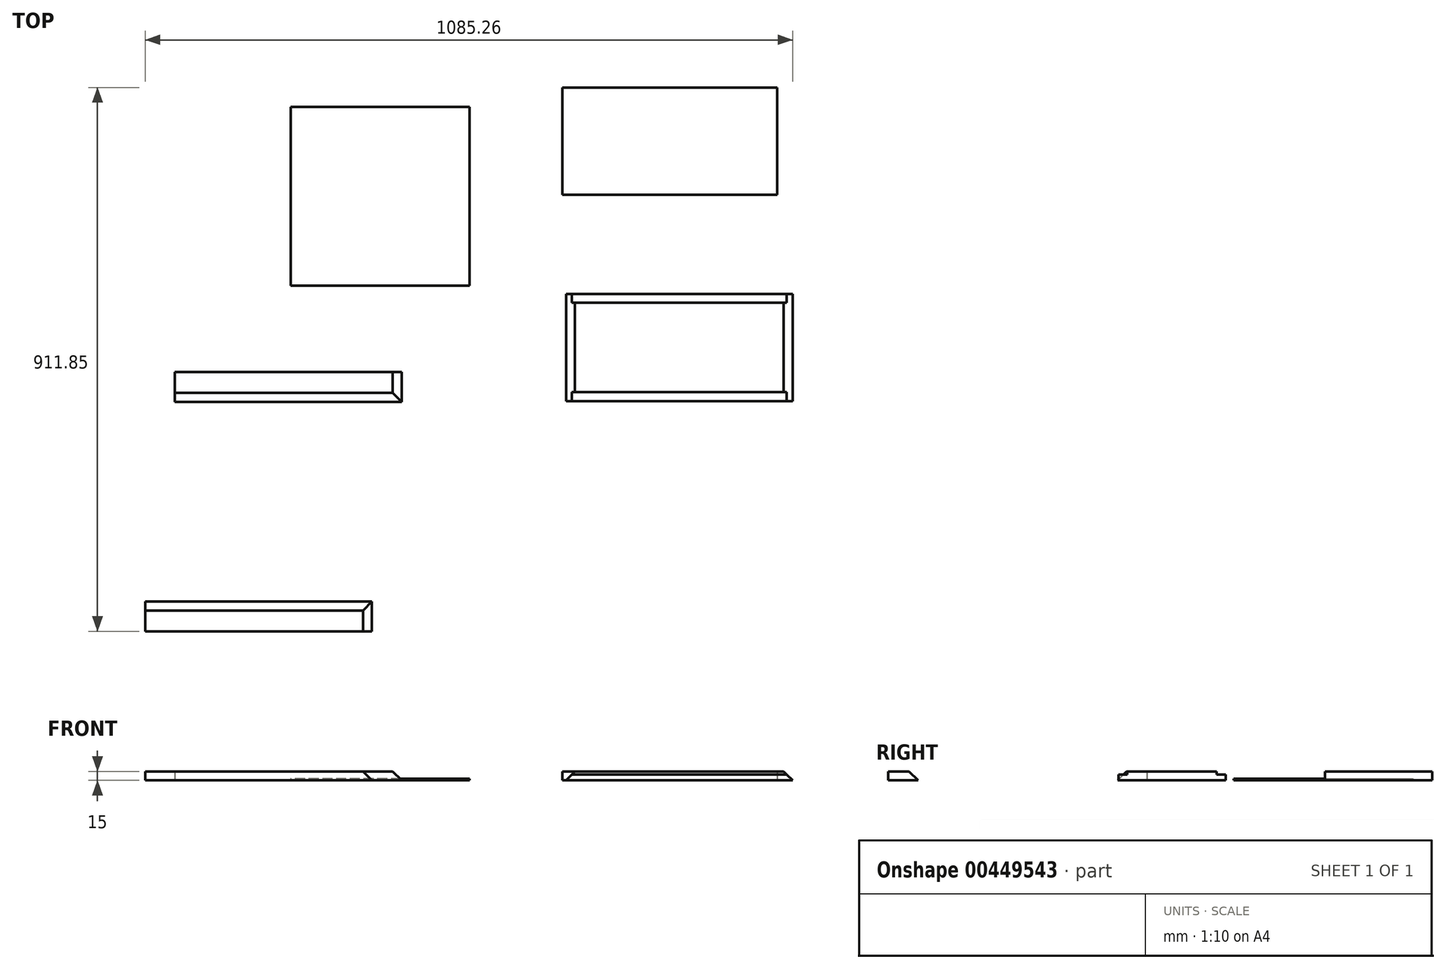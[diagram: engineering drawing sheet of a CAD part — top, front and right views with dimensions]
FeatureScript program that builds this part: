
annotation { "Feature Type Name" : "Feature", "Feature Type Description" : "" }
export const myFeature = defineFeature(function(context is Context, id is Id, definition is map)
    precondition{}
    {
        {
            var Q0;
            Q0=qCreatedBy(makeId("Top.planeOp"),FACE);
            var sketch = newSketch(context, id + "F0", { "sketchPlane" : qUnion([Q0])});
            skLineSegment(sketch, "E0.bottom", {"start": v(104.54, -6.9) * mm, "end": v(-255.46, -6.9) * mm});
            skLineSegment(sketch, "E0.top", {"start": v(104.54, 173.1) * mm, "end": v(-255.46, 173.1) * mm});
            skLineSegment(sketch, "E0.left", {"start": v(104.54, -6.9) * mm, "end": v(104.54, 173.1) * mm});
            skLineSegment(sketch, "E0.right", {"start": v(-255.46, -6.9) * mm, "end": v(-255.46, 173.1) * mm});
            skSolve(sketch);
        }
        {
            var Q0;
            Q0 = qSketchRegion(id + "F0", true);
            extrude(context, id + "F1", {"entities" : qUnion([Q0]), "depth" : 15 * mm});
        }
        {
            var Q0;
            Q0=qCreatedBy(makeId("Top.planeOp"),FACE);
            var sketch = newSketch(context, id + "F2", { "sketchPlane" : qUnion([Q0])});
            skLineSegment(sketch, "E1.bottom", {"start": v(-234.67, -172.9) * mm, "end": v(115.33, -172.9) * mm});
            skLineSegment(sketch, "E1.top", {"start": v(-234.67, -352.9) * mm, "end": v(115.33, -352.9) * mm});
            skLineSegment(sketch, "E1.left", {"start": v(-234.67, -172.9) * mm, "end": v(-234.67, -352.9) * mm});
            skLineSegment(sketch, "E1.right", {"start": v(115.33, -172.9) * mm, "end": v(115.33, -352.9) * mm});
            skSolve(sketch);
        }
        {
            var Q0;
            Q0 = qSketchRegion(id + "F2", true);
            extrude(context, id + "F3", {"entities" : qUnion([Q0]), "depth" : 15 * mm});
        }
        {
            var Q0;
            Q0=makeQuery(id+"F3.opExtrude","SWEPT_FACE",FACE,{"disambiguationData":[OSD([sQuery(id+"F2.wireOp",EDGE,"E1.top")])]});
            var sketch = newSketch(context, id + "F4", { "sketchPlane" : qUnion([Q0])});
            skLineSegment(sketch, "E2", {"start": v(-234.67, 0) * mm, "end": v(-249.67, 0) * mm});
            skLineSegment(sketch, "E3", {"start": v(-249.67, 0) * mm, "end": v(-234.67, 15) * mm});
            skLineSegment(sketch, "E4", {"start": v(115.33, 0) * mm, "end": v(130.33, 0) * mm});
            skLineSegment(sketch, "E5", {"start": v(130.33, 0) * mm, "end": v(115.33, 15) * mm});
            skSolve(sketch);
        }
        {
            var Q0;
            Q0 = qSketchRegion(id + "F4", true);
            var Q1;
            Q1=makeQuery(id+"F4.imprint","IMPRINT",FACE,{"disambiguationData":[TD([[makeQuery(id+"F4.imprint","IMPRINT",EDGE,{"derivedFrom":sQuery(id+"F4.wireOp",EDGE,"E2")}),-1.0]])]});
            var Q2;
            Q2=makeQuery(id+"F4.imprint","IMPRINT",FACE,{"disambiguationData":[TD([[makeQuery(id+"F4.imprint","IMPRINT",EDGE,{"derivedFrom":sQuery(id+"F4.wireOp",EDGE,"E4")}),1.0]])]});
            extrude(context, id + "F5", {"entities" : qUnion([Q0, Q1, Q2]), "operationType" : NewBodyOperationType.ADD, "oppositeDirection" : true, "depth" : 180 * mm});
        }
        {
            var Q0;
            Q0=makeQuery(id+"F3.opExtrude","CAP_FACE",FACE,{"disambiguationData":[OSD([sQuery(id+"F2.wireOp",EDGE,"E1.bottom"),sQuery(id+"F2.wireOp",EDGE,"E1.top"),sQuery(id+"F2.wireOp",EDGE,"E1.left"),sQuery(id+"F2.wireOp",EDGE,"E1.right")])],"isStart":false});
            var sketch = newSketch(context, id + "F6", { "sketchPlane" : qUnion([Q0])});
            skLineSegment(sketch, "E6.bottom", {"start": v(-234.67, -172.9) * mm, "end": v(115.33, -172.9) * mm});
            skLineSegment(sketch, "E6.top", {"start": v(-234.67, -187.9) * mm, "end": v(115.33, -187.9) * mm});
            skLineSegment(sketch, "E6.left", {"start": v(-234.67, -172.9) * mm, "end": v(-234.67, -187.9) * mm});
            skLineSegment(sketch, "E6.right", {"start": v(115.33, -172.9) * mm, "end": v(115.33, -187.9) * mm});
            skLineSegment(sketch, "E7.bottom", {"start": v(115.33, -187.9) * mm, "end": v(191.16, -187.9) * mm});
            skLineSegment(sketch, "E7.top", {"start": v(115.33, -172.9) * mm, "end": v(191.16, -172.9) * mm});
            skLineSegment(sketch, "E7.left", {"start": v(115.33, -187.9) * mm, "end": v(115.33, -172.9) * mm});
            skLineSegment(sketch, "E7.right", {"start": v(191.16, -187.9) * mm, "end": v(191.16, -172.9) * mm});
            skPoint(sketch, "E8.oppositeSnap0", {"position": v(-59.67, -172.9) * mm});
            skLineSegment(sketch, "E8.bottom", {"start": v(-234.67, -187.9) * mm, "end": v(-273.5, -187.9) * mm});
            skLineSegment(sketch, "E8.top", {"start": v(-234.67, -172.9) * mm, "end": v(-273.5, -172.9) * mm});
            skLineSegment(sketch, "E8.left", {"start": v(-234.67, -187.9) * mm, "end": v(-234.67, -172.9) * mm});
            skLineSegment(sketch, "E8.right", {"start": v(-273.5, -187.9) * mm, "end": v(-273.5, -172.9) * mm});
            skSolve(sketch);
        }
        {
            var Q0;
            Q0 = qSketchRegion(id + "F6", true);
            extrude(context, id + "F7", {"entities" : qUnion([Q0]), "operationType" : NewBodyOperationType.REMOVE, "oppositeDirection" : true, "depth" : 5 * mm});
        }
        {
            var Q0;
            Q0=makeQuery(id+"F3.opExtrude","CAP_FACE",FACE,{"disambiguationData":[OSD([sQuery(id+"F2.wireOp",EDGE,"E1.bottom"),sQuery(id+"F2.wireOp",EDGE,"E1.top"),sQuery(id+"F2.wireOp",EDGE,"E1.left"),sQuery(id+"F2.wireOp",EDGE,"E1.right")])],"isStart":false});
            var sketch = newSketch(context, id + "F8", { "sketchPlane" : qUnion([Q0])});
            skLineSegment(sketch, "E9.bottom", {"start": v(-234.67, -352.9) * mm, "end": v(115.33, -352.9) * mm});
            skLineSegment(sketch, "E9.top", {"start": v(-234.67, -337.9) * mm, "end": v(115.33, -337.9) * mm});
            skLineSegment(sketch, "E9.left", {"start": v(-234.67, -352.9) * mm, "end": v(-234.67, -337.9) * mm});
            skLineSegment(sketch, "E9.right", {"start": v(115.33, -352.9) * mm, "end": v(115.33, -337.9) * mm});
            skLineSegment(sketch, "E10.bottom", {"start": v(-234.67, -337.9) * mm, "end": v(-292.29, -337.9) * mm});
            skLineSegment(sketch, "E10.top", {"start": v(-234.67, -352.9) * mm, "end": v(-292.29, -352.9) * mm});
            skLineSegment(sketch, "E10.left", {"start": v(-234.67, -337.9) * mm, "end": v(-234.67, -352.9) * mm});
            skLineSegment(sketch, "E10.right", {"start": v(-292.29, -337.9) * mm, "end": v(-292.29, -352.9) * mm});
            skLineSegment(sketch, "E11.bottom", {"start": v(115.33, -337.9) * mm, "end": v(169.6, -337.9) * mm});
            skLineSegment(sketch, "E11.top", {"start": v(115.33, -352.9) * mm, "end": v(169.6, -352.9) * mm});
            skLineSegment(sketch, "E11.left", {"start": v(115.33, -337.9) * mm, "end": v(115.33, -352.9) * mm});
            skLineSegment(sketch, "E11.right", {"start": v(169.6, -337.9) * mm, "end": v(169.6, -352.9) * mm});
            skSolve(sketch);
        }
        {
            var Q0;
            Q0 = qSketchRegion(id + "F8", true);
            extrude(context, id + "F9", {"entities" : qUnion([Q0]), "operationType" : NewBodyOperationType.REMOVE, "oppositeDirection" : true, "depth" : 5 * mm});
        }
        {
            var Q0;
            Q0=qCreatedBy(makeId("Top.planeOp"),FACE);
            var sketch = newSketch(context, id + "F10", { "sketchPlane" : qUnion([Q0])});
            skLineSegment(sketch, "E12.bottom", {"start": v(-411.2, -159.37) * mm, "end": v(-711.2, -159.37) * mm});
            skLineSegment(sketch, "E12.top", {"start": v(-411.2, 140.63) * mm, "end": v(-711.2, 140.63) * mm});
            skLineSegment(sketch, "E12.left", {"start": v(-411.2, -159.37) * mm, "end": v(-411.2, 140.63) * mm});
            skLineSegment(sketch, "E12.right", {"start": v(-711.2, -159.37) * mm, "end": v(-711.2, 140.63) * mm});
            skSolve(sketch);
        }
        {
            var Q0;
            Q0 = qSketchRegion(id + "F10", true);
            extrude(context, id + "F11", {"entities" : qUnion([Q0]), "depth" : 3 * mm});
        }
        {
            var Q0;
            Q0=qCreatedBy(makeId("Top.planeOp"),FACE);
            var sketch = newSketch(context, id + "F12", { "sketchPlane" : qUnion([Q0])});
            skLineSegment(sketch, "E13.bottom", {"start": v(-525.04, -354.14) * mm, "end": v(-905.04, -354.14) * mm});
            skLineSegment(sketch, "E13.top", {"start": v(-525.04, -304.14) * mm, "end": v(-905.04, -304.14) * mm});
            skLineSegment(sketch, "E13.left", {"start": v(-525.04, -354.14) * mm, "end": v(-525.04, -304.14) * mm});
            skLineSegment(sketch, "E13.right", {"start": v(-905.04, -354.14) * mm, "end": v(-905.04, -304.14) * mm});
            skSolve(sketch);
        }
        {
            var Q0;
            Q0 = qSketchRegion(id + "F12", true);
            extrude(context, id + "F13", {"entities" : qUnion([Q0]), "depth" : 15 * mm});
        }
        {
            var Q0;
            Q0=makeQuery(id+"F13.opExtrude","SWEPT_FACE",FACE,{"disambiguationData":[OSD([sQuery(id+"F12.wireOp",EDGE,"E13.left")])]});
            var sketch = newSketch(context, id + "F14", { "sketchPlane" : qUnion([Q0])});
            skLineSegment(sketch, "E14.bottom", {"start": v(-354.14, 0) * mm, "end": v(-339.14, 0) * mm});
            skLineSegment(sketch, "E14.top", {"start": v(-354.14, 15) * mm, "end": v(-339.14, 15) * mm});
            skLineSegment(sketch, "E14.left", {"start": v(-354.14, 0) * mm, "end": v(-354.14, 15) * mm});
            skLineSegment(sketch, "E14.right", {"start": v(-339.14, 0) * mm, "end": v(-339.14, 15) * mm});
            skLineSegment(sketch, "E15", {"start": v(-354.14, 0) * mm, "end": v(-339.14, 15) * mm});
            skSolve(sketch);
        }
        {
            var Q0;
            Q0=makeQuery(id+"F14.imprint","IMPRINT",FACE,{"disambiguationData":[TD([[makeQuery(id+"F14.imprint","IMPRINT",EDGE,{"derivedFrom":sQuery(id+"F14.wireOp",EDGE,"E14.top")}),-1.0]])]});
            extrude(context, id + "F15", {"entities" : qUnion([Q0]), "operationType" : NewBodyOperationType.REMOVE, "oppositeDirection" : true, "depth" : 551 * mm});
        }
        {
            var Q0;
            Q0=makeQuery(id+"F13.opExtrude","SWEPT_FACE",FACE,{"disambiguationData":[OSD([sQuery(id+"F12.wireOp",EDGE,"E13.top")])]});
            var sketch = newSketch(context, id + "F16", { "sketchPlane" : qUnion([Q0])});
            skLineSegment(sketch, "E16.bottom", {"start": v(525.04, 0) * mm, "end": v(540.04, 0) * mm});
            skLineSegment(sketch, "E16.top", {"start": v(525.04, 15) * mm, "end": v(540.04, 15) * mm});
            skLineSegment(sketch, "E16.left", {"start": v(525.04, 0) * mm, "end": v(525.04, 15) * mm});
            skLineSegment(sketch, "E16.right", {"start": v(540.04, 0) * mm, "end": v(540.04, 15) * mm});
            skLineSegment(sketch, "E17", {"start": v(525.04, 0) * mm, "end": v(540.04, 15) * mm});
            skSolve(sketch);
        }
        {
            var Q0;
            Q0=makeQuery(id+"F16.imprint","IMPRINT",FACE,{"disambiguationData":[TD([[makeQuery(id+"F16.imprint","IMPRINT",EDGE,{"derivedFrom":sQuery(id+"F16.wireOp",EDGE,"E16.top")}),-1.0]])]});
            extrude(context, id + "F17", {"entities" : qUnion([Q0]), "operationType" : NewBodyOperationType.REMOVE, "oppositeDirection" : true, "depth" : 79 * mm});
        }
        {
            var Q0;
            Q0=qCreatedBy(makeId("Top.planeOp"),FACE);
            var sketch = newSketch(context, id + "F18", { "sketchPlane" : qUnion([Q0])});
            skLineSegment(sketch, "E18.bottom", {"start": v(-574.93, -688.75) * mm, "end": v(-954.93, -688.75) * mm});
            skLineSegment(sketch, "E18.top", {"start": v(-574.93, -738.75) * mm, "end": v(-954.93, -738.75) * mm});
            skLineSegment(sketch, "E18.left", {"start": v(-574.93, -688.75) * mm, "end": v(-574.93, -738.75) * mm});
            skLineSegment(sketch, "E18.right", {"start": v(-954.93, -688.75) * mm, "end": v(-954.93, -738.75) * mm});
            skSolve(sketch);
        }
        {
            var Q0;
            Q0 = qSketchRegion(id + "F18", true);
            extrude(context, id + "F19", {"entities" : qUnion([Q0]), "depth" : 15 * mm});
        }
        {
            var Q0;
            Q0=makeQuery(id+"F19.opExtrude","SWEPT_FACE",FACE,{"disambiguationData":[OSD([sQuery(id+"F18.wireOp",EDGE,"E18.bottom")])]});
            var sketch = newSketch(context, id + "F20", { "sketchPlane" : qUnion([Q0])});
            skLineSegment(sketch, "E19.bottom", {"start": v(574.93, 0) * mm, "end": v(589.93, 0) * mm});
            skLineSegment(sketch, "E19.top", {"start": v(574.93, 15) * mm, "end": v(589.93, 15) * mm});
            skLineSegment(sketch, "E19.left", {"start": v(574.93, 0) * mm, "end": v(574.93, 15) * mm});
            skLineSegment(sketch, "E19.right", {"start": v(589.93, 0) * mm, "end": v(589.93, 15) * mm});
            skLineSegment(sketch, "E20", {"start": v(574.93, 0) * mm, "end": v(589.93, 15) * mm});
            skSolve(sketch);
        }
        {
            var Q0;
            Q0=makeQuery(id+"F20.imprint","IMPRINT",FACE,{"disambiguationData":[TD([[makeQuery(id+"F20.imprint","IMPRINT",EDGE,{"derivedFrom":sQuery(id+"F20.wireOp",EDGE,"E19.top")}),-1.0]])]});
            extrude(context, id + "F21", {"entities" : qUnion([Q0]), "operationType" : NewBodyOperationType.REMOVE, "oppositeDirection" : true, "depth" : 76 * mm});
        }
        {
            var Q0;
            Q0=makeQuery(id+"F19.opExtrude","SWEPT_FACE",FACE,{"disambiguationData":[OSD([sQuery(id+"F18.wireOp",EDGE,"E18.right")])]});
            var sketch = newSketch(context, id + "F22", { "sketchPlane" : qUnion([Q0])});
            skLineSegment(sketch, "E21.bottom", {"start": v(688.75, 0) * mm, "end": v(703.75, 0) * mm});
            skLineSegment(sketch, "E21.top", {"start": v(688.75, 15) * mm, "end": v(703.75, 15) * mm});
            skLineSegment(sketch, "E21.left", {"start": v(688.75, 0) * mm, "end": v(688.75, 15) * mm});
            skLineSegment(sketch, "E21.right", {"start": v(703.75, 0) * mm, "end": v(703.75, 15) * mm});
            skLineSegment(sketch, "E22", {"start": v(688.75, 0) * mm, "end": v(703.75, 15) * mm});
            skSolve(sketch);
        }
        {
            var Q0;
            Q0=makeQuery(id+"F22.imprint","IMPRINT",FACE,{"disambiguationData":[TD([[makeQuery(id+"F22.imprint","IMPRINT",EDGE,{"derivedFrom":sQuery(id+"F22.wireOp",EDGE,"E21.top")}),-1.0]])]});
            extrude(context, id + "F23", {"entities" : qUnion([Q0]), "operationType" : NewBodyOperationType.REMOVE, "oppositeDirection" : true, "depth" : 513.3 * mm});
        }
    });
